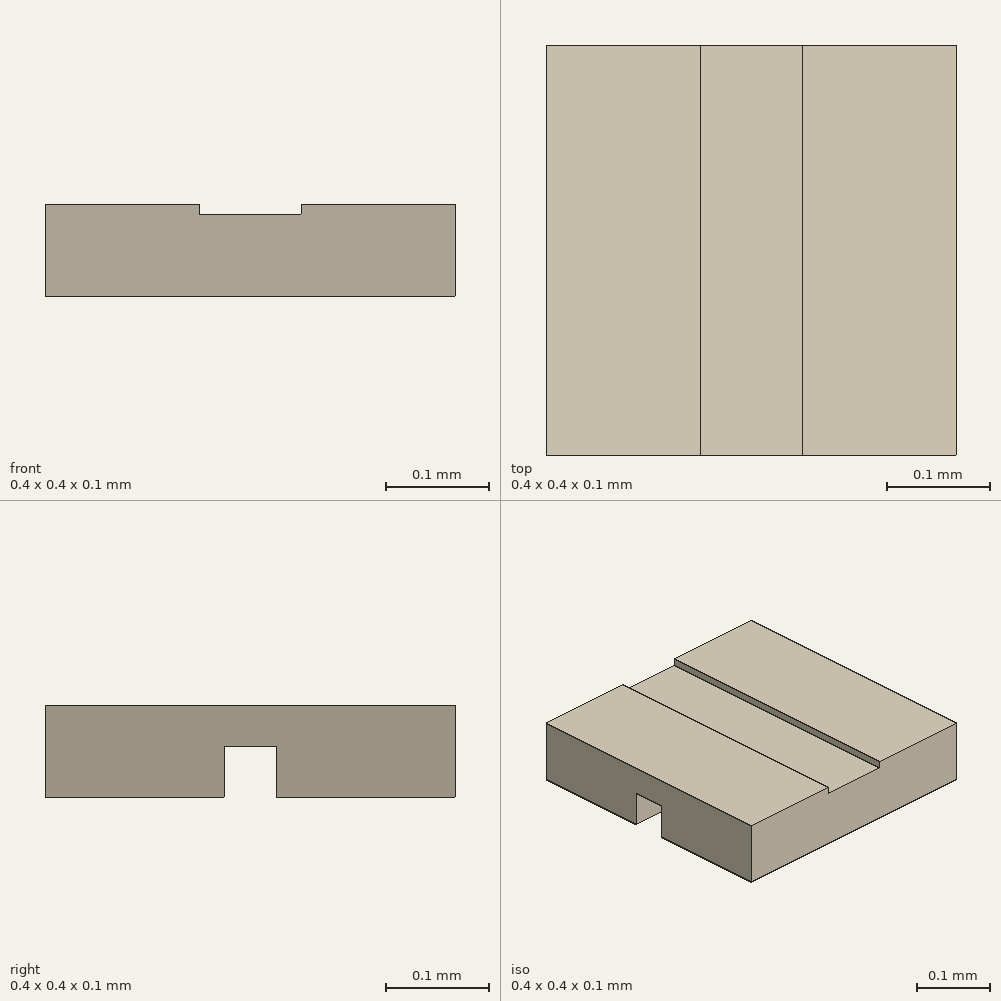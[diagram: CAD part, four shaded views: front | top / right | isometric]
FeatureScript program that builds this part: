
annotation { "Feature Type Name" : "Feature", "Feature Type Description" : "" }
export const myFeature = defineFeature(function(context is Context, id is Id, definition is map)
    precondition{}
    {
        {
            var Q0;
            Q0=qCreatedBy(makeId("Top.planeOp"),FACE);
            var sketch = newSketch(context, id + "F0", { "sketchPlane" : qUnion([Q0])});
            skLineSegment(sketch, "E0.bottom", {"start": v(0, 0) * mm, "end": v(0.4, 0) * mm});
            skLineSegment(sketch, "E0.top", {"start": v(0, 0.4) * mm, "end": v(0.4, 0.4) * mm});
            skLineSegment(sketch, "E0.left", {"start": v(0, 0) * mm, "end": v(0, 0.4) * mm});
            skLineSegment(sketch, "E0.right", {"start": v(0.4, 0) * mm, "end": v(0.4, 0.4) * mm});
            skSolve(sketch);
        }
        {
            var Q0;
            Q0=makeQuery(id+"F0.imprint","IMPRINT",FACE,{"disambiguationData":[TD([[makeQuery(id+"F0.imprint","IMPRINT",EDGE,{"derivedFrom":sQuery(id+"F0.wireOp",EDGE,"E0.bottom")}),1.0]])]});
            extrude(context, id + "F1", {"entities" : qUnion([Q0]), "depth" : 0.09 * mm});
        }
        {
            var Q0;
            Q0=makeQuery(id+"F1.opExtrude","SWEPT_FACE",FACE,{"disambiguationData":[OSD([sQuery(id+"F0.wireOp",EDGE,"E0.right")])]});
            var sketch = newSketch(context, id + "F2", { "sketchPlane" : qUnion([Q0])});
            skLineSegment(sketch, "E1.bottom", {"start": v(0.17, 0) * mm, "end": v(0.23, 0) * mm});
            skLineSegment(sketch, "E1.top", {"start": v(0.17, 0.05) * mm, "end": v(0.23, 0.05) * mm});
            skLineSegment(sketch, "E1.left", {"start": v(0.17, 0) * mm, "end": v(0.17, 0.05) * mm});
            skLineSegment(sketch, "E1.right", {"start": v(0.23, 0) * mm, "end": v(0.23, 0.05) * mm});
            skSolve(sketch);
        }
        {
            var Q0;
            Q0 = qSketchRegion(id + "F2", true);
            extrude(context, id + "F3", {"entities" : qUnion([Q0]), "operationType" : NewBodyOperationType.REMOVE, "endBound" : BoundingType.THROUGH_ALL, "oppositeDirection" : true, "depth" : 0.4 * mm});
        }
        {
            var Q0;
            Q0=makeQuery(id+"F1.opExtrude","SWEPT_FACE",FACE,{"disambiguationData":[OSD([sQuery(id+"F0.wireOp",EDGE,"E0.top")])]});
            var sketch = newSketch(context, id + "F4", { "sketchPlane" : qUnion([Q0])});
            skLineSegment(sketch, "E2.bottom", {"start": v(-0.25, 0.09) * mm, "end": v(-0.15, 0.09) * mm});
            skLineSegment(sketch, "E2.top", {"start": v(-0.25, 0.08) * mm, "end": v(-0.15, 0.08) * mm});
            skLineSegment(sketch, "E2.left", {"start": v(-0.25, 0.09) * mm, "end": v(-0.25, 0.08) * mm});
            skLineSegment(sketch, "E2.right", {"start": v(-0.15, 0.09) * mm, "end": v(-0.15, 0.08) * mm});
            skSolve(sketch);
        }
        {
            var Q0;
            Q0=makeQuery(id+"F4.imprint","IMPRINT",FACE,{"disambiguationData":[TD([[makeQuery(id+"F4.imprint","IMPRINT",EDGE,{"derivedFrom":sQuery(id+"F4.wireOp",EDGE,"E2.bottom")}),1.0]])]});
            extrude(context, id + "F5", {"entities" : qUnion([Q0]), "operationType" : NewBodyOperationType.REMOVE, "endBound" : BoundingType.THROUGH_ALL, "oppositeDirection" : true, "depth" : 25 * mm});
        }
    });
